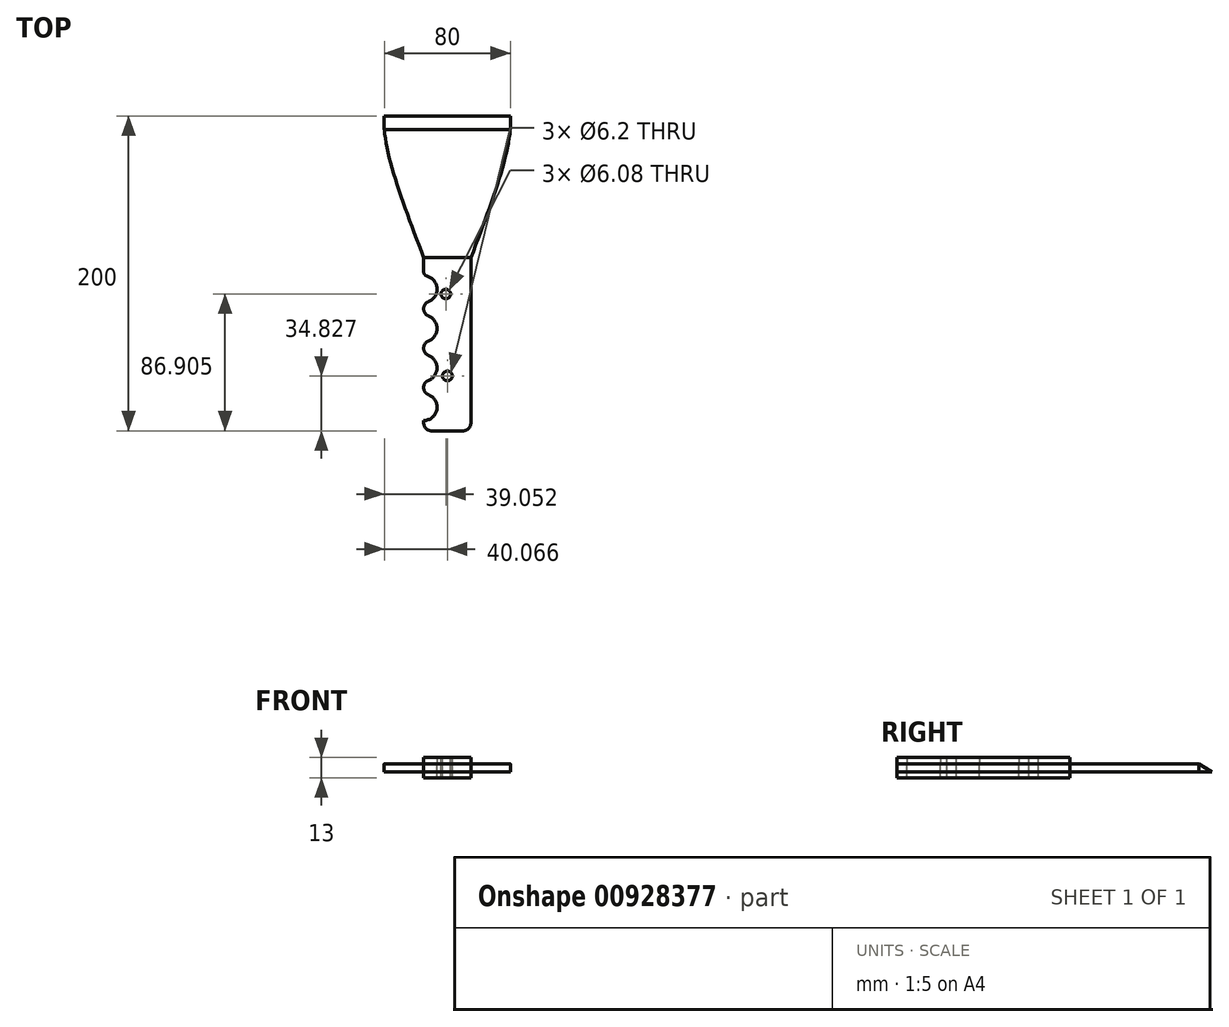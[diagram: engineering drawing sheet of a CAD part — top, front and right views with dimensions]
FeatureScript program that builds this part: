
annotation { "Feature Type Name" : "Feature", "Feature Type Description" : "" }
export const myFeature = defineFeature(function(context is Context, id is Id, definition is map)
    precondition{}
    {
        {
            var Q0;
            Q0=qCreatedBy(makeId("Top.planeOp"),FACE);
            var sketch = newSketch(context, id + "F0", { "sketchPlane" : qUnion([Q0])});
            skLineSegment(sketch, "E0.bottom", {"start": v(-36.21, -52.82) * mm, "end": v(43.79, -52.82) * mm});
            skLineSegment(sketch, "E0.top", {"start": v(-36.21, 147.18) * mm, "end": v(43.79, 147.18) * mm});
            skLineSegment(sketch, "E0.left", {"start": v(-36.21, -52.82) * mm, "end": v(-36.21, 147.18) * mm});
            skLineSegment(sketch, "E0.right", {"start": v(43.79, -52.82) * mm, "end": v(43.79, 147.18) * mm});
            skLineSegment(sketch, "E1.0", {"start": v(-36.21, 57.18) * mm, "end": v(43.79, 57.18) * mm});
            skLineSegment(sketch, "E2.0", {"start": v(18.79, -52.82) * mm, "end": v(18.79, 147.18) * mm});
            skLineSegment(sketch, "E3.0", {"start": v(-11.21, -52.82) * mm, "end": v(-11.21, 147.18) * mm});
            skFitSpline(sketch, "E4", {"points": [v(18.79, 57.18) * mm, v(43.79, 147.18) * mm, v(32.99, 168.62) * mm], "startDerivative": vector(60.83, 159.48) * mm, "endDerivative": vector(-43.84, 51.63) * mm});
            skFitSpline(sketch, "E5", {"points": [v(-11.21, 57.18) * mm, v(-36.21, 147.18) * mm, v(-25.14, 169.08) * mm], "startDerivative": vector(-61.11, 159.77) * mm, "endDerivative": vector(44.62, 52.51) * mm});
            skSolve(sketch);
        }
        {
            var Q0;
            {var subQ2=sQuery(id+"F0.wireOp",EDGE,"E0.top");var subQ4=sQuery(id+"F0.wireOp",EDGE,"E3.0");var subQ5=makeQuery(id+"F0.imprint","INTERSECT",VERTEX,{"derivedFrom":[subQ2,subQ4]});Q0=makeQuery(id+"F0.imprint","IMPRINT",FACE,{"disambiguationData":[TD([[makeQuery(id+"F0.imprint","IMPRINT",EDGE,{"disambiguationData":[TD([[subQ5,1.0]])],"derivedFrom":subQ2}),-1.0]])]});}
            var Q1;
            {var subQ0=sQuery(id+"F0.wireOp",EDGE,"E2.0");var subQ1=sQuery(id+"F0.wireOp",EDGE,"E0.top");var subQ2=makeQuery(id+"F0.imprint","INTERSECT",VERTEX,{"derivedFrom":[subQ1,subQ0]});Q1=makeQuery(id+"F0.imprint","IMPRINT",FACE,{"disambiguationData":[TD([[makeQuery(id+"F0.imprint","IMPRINT",EDGE,{"disambiguationData":[TD([[subQ2,1.0]])],"derivedFrom":subQ1}),-1.0]])]});}
            var Q2;
            {var subQ2=sQuery(id+"F0.wireOp",EDGE,"E0.top");var subQ4=sQuery(id+"F0.wireOp",EDGE,"E2.0");var subQ5=makeQuery(id+"F0.imprint","INTERSECT",VERTEX,{"derivedFrom":[subQ2,subQ4]});Q2=makeQuery(id+"F0.imprint","IMPRINT",FACE,{"disambiguationData":[TD([[makeQuery(id+"F0.imprint","IMPRINT",EDGE,{"disambiguationData":[TD([[subQ5,-1.0]])],"derivedFrom":subQ2}),-1.0]])]});}
            var Q3;
            {var subQ0=sQuery(id+"F0.wireOp",EDGE,"E2.0");var subQ1=sQuery(id+"F0.wireOp",EDGE,"E0.bottom");var subQ2=makeQuery(id+"F0.imprint","INTERSECT",VERTEX,{"derivedFrom":[subQ1,subQ0]});Q3=makeQuery(id+"F0.imprint","IMPRINT",FACE,{"disambiguationData":[TD([[makeQuery(id+"F0.imprint","IMPRINT",EDGE,{"disambiguationData":[TD([[subQ2,1.0]])],"derivedFrom":subQ1}),1.0]])]});}
            extrude(context, id + "F1", {"entities" : qUnion([Q0, Q1, Q2, Q3]), "depth" : 5 * mm, "offsetDistance" : 25 * mm});
        }
        {
            var Q0;
            Q0=makeQuery(id+"F1.opExtrude","CAP_FACE",FACE,{"disambiguationData":[OSD([sQuery(id+"F0.wireOp",EDGE,"E0.bottom"),sQuery(id+"F0.wireOp",EDGE,"E0.top"),sQuery(id+"F0.wireOp",EDGE,"E0.left"),sQuery(id+"F0.wireOp",EDGE,"E0.right"),sQuery(id+"F0.wireOp",EDGE,"E2.0"),sQuery(id+"F0.wireOp",EDGE,"E3.0"),sQuery(id+"F0.wireOp",EDGE,"E4"),sQuery(id+"F0.wireOp",EDGE,"E5")])],"isStart":false});
            var sketch = newSketch(context, id + "F2", { "sketchPlane" : qUnion([Q0])});
            skCircle(sketch, "E6", {"center": v(-11.21, 37.18) * mm, "radius": 8.5 * mm});
            skCircle(sketch, "E7", {"center": v(-11.21, 12.18) * mm, "radius": 8.5 * mm});
            skCircle(sketch, "E8", {"center": v(-11.21, -12.82) * mm, "radius": 8.5 * mm});
            skCircle(sketch, "E9", {"center": v(-11.21, -37.82) * mm, "radius": 8.5 * mm});
            skSolve(sketch);
        }
        {
            var Q0;
            Q0=makeQuery(id+"F1.opExtrude","SWEPT_EDGE",EDGE,{"disambiguationData":[OSD([sQuery(id+"F0.wireOp",EDGE,"E0.bottom"),sQuery(id+"F0.wireOp",EDGE,"E3.0")])]});
            var Q1;
            Q1=makeQuery(id+"F1.opExtrude","SWEPT_EDGE",EDGE,{"disambiguationData":[OSD([sQuery(id+"F0.wireOp",EDGE,"E0.bottom"),sQuery(id+"F0.wireOp",EDGE,"E2.0")])]});
            fillet(context, id + "F3", {"entities" : qUnion([Q0, Q1]), "radius" : 5 * mm, "tangentPropagation" : true, "allowEdgeOverflow" : false});
        }
        {
            var Q0;
            {var subQ0=sQuery(id+"F2.wireOp",EDGE,"E6");var subQ1=makeQuery(id+"F1.opExtrude","CAP_EDGE",EDGE,{"disambiguationData":[OSD([sQuery(id+"F0.wireOp",EDGE,"E3.0")])],"isStart":false});var subQ2=makeQuery(id+"F2.imprint","INTERSECT",VERTEX,{"disambiguationData":[OD(0.0)],"derivedFrom":[subQ1,subQ0]});Q0=makeQuery(id+"F2.imprint","IMPRINT",FACE,{"disambiguationData":[TD([[makeQuery(id+"F2.imprint","IMPRINT",EDGE,{"disambiguationData":[TD([[subQ2,1.0]])],"derivedFrom":subQ0}),1.0]])]});}
            var Q1;
            {var subQ0=sQuery(id+"F2.wireOp",EDGE,"E7");var subQ1=makeQuery(id+"F1.opExtrude","CAP_EDGE",EDGE,{"disambiguationData":[OSD([sQuery(id+"F0.wireOp",EDGE,"E3.0")])],"isStart":false});var subQ2=makeQuery(id+"F2.imprint","INTERSECT",VERTEX,{"disambiguationData":[OD(0.0)],"derivedFrom":[subQ1,subQ0]});Q1=makeQuery(id+"F2.imprint","IMPRINT",FACE,{"disambiguationData":[TD([[makeQuery(id+"F2.imprint","IMPRINT",EDGE,{"disambiguationData":[TD([[subQ2,1.0]])],"derivedFrom":subQ0}),1.0]])]});}
            var Q2;
            {var subQ0=sQuery(id+"F2.wireOp",EDGE,"E8");var subQ1=makeQuery(id+"F1.opExtrude","CAP_EDGE",EDGE,{"disambiguationData":[OSD([sQuery(id+"F0.wireOp",EDGE,"E3.0")])],"isStart":false});var subQ2=makeQuery(id+"F2.imprint","INTERSECT",VERTEX,{"disambiguationData":[OD(0.0)],"derivedFrom":[subQ1,subQ0]});Q2=makeQuery(id+"F2.imprint","IMPRINT",FACE,{"disambiguationData":[TD([[makeQuery(id+"F2.imprint","IMPRINT",EDGE,{"disambiguationData":[TD([[subQ2,-1.0]])],"derivedFrom":subQ0}),1.0]])]});}
            var Q3;
            {var subQ0=sQuery(id+"F2.wireOp",EDGE,"E9");var subQ1=makeQuery(id+"F1.opExtrude","CAP_EDGE",EDGE,{"disambiguationData":[OSD([sQuery(id+"F0.wireOp",EDGE,"E3.0")])],"isStart":false});var subQ2=makeQuery(id+"F2.imprint","INTERSECT",VERTEX,{"disambiguationData":[OD(0.0)],"derivedFrom":[subQ1,subQ0]});Q3=makeQuery(id+"F2.imprint","IMPRINT",FACE,{"disambiguationData":[TD([[makeQuery(id+"F2.imprint","IMPRINT",EDGE,{"disambiguationData":[TD([[subQ2,-1.0]])],"derivedFrom":subQ0}),1.0]])]});}
            extrude(context, id + "F4", {"entities" : qUnion([Q0, Q1, Q2, Q3]), "operationType" : NewBodyOperationType.REMOVE, "oppositeDirection" : true, "depth" : 25 * mm, "offsetDistance" : 25 * mm});
        }
        {
            var Q0;
            {var subQ0=sQuery(id+"F2.wireOp",EDGE,"E8");var subQ1=sQuery(id+"F0.wireOp",EDGE,"E3.0");Q0=makeQuery(id+"F4.boolean.opBoolean","COPY",EDGE,{"derivedFrom":makeQuery(id+"F4.opExtrude","SWEPT_EDGE",EDGE,{"disambiguationData":[OSD([subQ1,subQ0]),TDD([makeQuery(id+"F2.imprint","INTERSECT",VERTEX,{"disambiguationData":[OD(1.0)],"derivedFrom":[makeQuery(id+"F1.opExtrude","CAP_EDGE",EDGE,{"disambiguationData":[OSD([subQ1])],"isStart":false}),subQ0]})])]})});}
            var Q1;
            {var subQ0=sQuery(id+"F2.wireOp",EDGE,"E7");var subQ1=sQuery(id+"F0.wireOp",EDGE,"E3.0");Q1=makeQuery(id+"F4.boolean.opBoolean","COPY",EDGE,{"derivedFrom":makeQuery(id+"F4.opExtrude","SWEPT_EDGE",EDGE,{"disambiguationData":[OSD([subQ1,subQ0]),TDD([makeQuery(id+"F2.imprint","INTERSECT",VERTEX,{"disambiguationData":[OD(1.0)],"derivedFrom":[makeQuery(id+"F1.opExtrude","CAP_EDGE",EDGE,{"disambiguationData":[OSD([subQ1])],"isStart":false}),subQ0]})])]})});}
            var Q2;
            {var subQ0=sQuery(id+"F2.wireOp",EDGE,"E8");var subQ1=sQuery(id+"F0.wireOp",EDGE,"E3.0");Q2=makeQuery(id+"F4.boolean.opBoolean","COPY",EDGE,{"derivedFrom":makeQuery(id+"F4.opExtrude","SWEPT_EDGE",EDGE,{"disambiguationData":[OSD([subQ1,subQ0]),TDD([makeQuery(id+"F2.imprint","INTERSECT",VERTEX,{"disambiguationData":[OD(0.0)],"derivedFrom":[makeQuery(id+"F1.opExtrude","CAP_EDGE",EDGE,{"disambiguationData":[OSD([subQ1])],"isStart":false}),subQ0]})])]})});}
            var Q3;
            {var subQ0=sQuery(id+"F2.wireOp",EDGE,"E9");var subQ1=sQuery(id+"F0.wireOp",EDGE,"E3.0");Q3=makeQuery(id+"F4.boolean.opBoolean","COPY",EDGE,{"derivedFrom":makeQuery(id+"F4.opExtrude","SWEPT_EDGE",EDGE,{"disambiguationData":[OSD([subQ1,subQ0]),TDD([makeQuery(id+"F2.imprint","INTERSECT",VERTEX,{"disambiguationData":[OD(1.0)],"derivedFrom":[makeQuery(id+"F1.opExtrude","CAP_EDGE",EDGE,{"disambiguationData":[OSD([subQ1])],"isStart":false}),subQ0]})])]})});}
            var Q4;
            {var subQ0=sQuery(id+"F2.wireOp",EDGE,"E9");var subQ1=sQuery(id+"F0.wireOp",EDGE,"E3.0");Q4=makeQuery(id+"F4.boolean.opBoolean","COPY",EDGE,{"derivedFrom":makeQuery(id+"F4.opExtrude","SWEPT_EDGE",EDGE,{"disambiguationData":[OSD([subQ1,subQ0]),TDD([makeQuery(id+"F2.imprint","INTERSECT",VERTEX,{"disambiguationData":[OD(0.0)],"derivedFrom":[makeQuery(id+"F1.opExtrude","CAP_EDGE",EDGE,{"disambiguationData":[OSD([subQ1])],"isStart":false}),subQ0]})])]})});}
            var Q5;
            {var subQ0=sQuery(id+"F2.wireOp",EDGE,"E7");var subQ1=sQuery(id+"F0.wireOp",EDGE,"E3.0");Q5=makeQuery(id+"F4.boolean.opBoolean","COPY",EDGE,{"derivedFrom":makeQuery(id+"F4.opExtrude","SWEPT_EDGE",EDGE,{"disambiguationData":[OSD([subQ1,subQ0]),TDD([makeQuery(id+"F2.imprint","INTERSECT",VERTEX,{"disambiguationData":[OD(0.0)],"derivedFrom":[makeQuery(id+"F1.opExtrude","CAP_EDGE",EDGE,{"disambiguationData":[OSD([subQ1])],"isStart":false}),subQ0]})])]})});}
            var Q6;
            {var subQ0=sQuery(id+"F2.wireOp",EDGE,"E6");var subQ1=sQuery(id+"F0.wireOp",EDGE,"E3.0");Q6=makeQuery(id+"F4.boolean.opBoolean","COPY",EDGE,{"derivedFrom":makeQuery(id+"F4.opExtrude","SWEPT_EDGE",EDGE,{"disambiguationData":[OSD([subQ1,subQ0]),TDD([makeQuery(id+"F2.imprint","INTERSECT",VERTEX,{"disambiguationData":[OD(1.0)],"derivedFrom":[makeQuery(id+"F1.opExtrude","CAP_EDGE",EDGE,{"disambiguationData":[OSD([subQ1])],"isStart":false}),subQ0]})])]})});}
            fillet(context, id + "F5", {"entities" : qUnion([Q0, Q1, Q2, Q3, Q4, Q5, Q6]), "radius" : 5 * mm, "tangentPropagation" : true, "allowEdgeOverflow" : false});
        }
        {
            var Q0;
            {var subQ0=sQuery(id+"F2.wireOp",EDGE,"E8");var subQ1=sQuery(id+"F0.wireOp",EDGE,"E3.0");Q0=makeQuery(id+"F4.boolean.opBoolean","COPY",EDGE,{"derivedFrom":makeQuery(id+"F4.opExtrude","SWEPT_EDGE",EDGE,{"disambiguationData":[OSD([subQ1,subQ0]),TDD([makeQuery(id+"F2.imprint","INTERSECT",VERTEX,{"disambiguationData":[OD(0.0)],"derivedFrom":[makeQuery(id+"F1.opExtrude","CAP_EDGE",EDGE,{"disambiguationData":[OSD([subQ1])],"isStart":false}),subQ0]})])]})});}
            var Q1;
            {var subQ0=sQuery(id+"F2.wireOp",EDGE,"E9");var subQ1=sQuery(id+"F0.wireOp",EDGE,"E3.0");Q1=makeQuery(id+"F4.boolean.opBoolean","COPY",EDGE,{"derivedFrom":makeQuery(id+"F4.opExtrude","SWEPT_EDGE",EDGE,{"disambiguationData":[OSD([subQ1,subQ0]),TDD([makeQuery(id+"F2.imprint","INTERSECT",VERTEX,{"disambiguationData":[OD(1.0)],"derivedFrom":[makeQuery(id+"F1.opExtrude","CAP_EDGE",EDGE,{"disambiguationData":[OSD([subQ1])],"isStart":false}),subQ0]})])]})});}
            var Q2;
            {var subQ0=sQuery(id+"F2.wireOp",EDGE,"E9");var subQ1=sQuery(id+"F0.wireOp",EDGE,"E3.0");Q2=makeQuery(id+"F4.boolean.opBoolean","COPY",EDGE,{"derivedFrom":makeQuery(id+"F4.opExtrude","SWEPT_EDGE",EDGE,{"disambiguationData":[OSD([subQ1,subQ0]),TDD([makeQuery(id+"F2.imprint","INTERSECT",VERTEX,{"disambiguationData":[OD(0.0)],"derivedFrom":[makeQuery(id+"F1.opExtrude","CAP_EDGE",EDGE,{"disambiguationData":[OSD([subQ1])],"isStart":false}),subQ0]})])]})});}
            var Q3;
            {var subQ0=sQuery(id+"F2.wireOp",EDGE,"E7");var subQ1=sQuery(id+"F0.wireOp",EDGE,"E3.0");Q3=makeQuery(id+"F4.boolean.opBoolean","COPY",EDGE,{"derivedFrom":makeQuery(id+"F4.opExtrude","SWEPT_EDGE",EDGE,{"disambiguationData":[OSD([subQ1,subQ0]),TDD([makeQuery(id+"F2.imprint","INTERSECT",VERTEX,{"disambiguationData":[OD(1.0)],"derivedFrom":[makeQuery(id+"F1.opExtrude","CAP_EDGE",EDGE,{"disambiguationData":[OSD([subQ1])],"isStart":false}),subQ0]})])]})});}
            var Q4;
            {var subQ0=sQuery(id+"F2.wireOp",EDGE,"E8");var subQ1=sQuery(id+"F0.wireOp",EDGE,"E3.0");Q4=makeQuery(id+"F4.boolean.opBoolean","COPY",EDGE,{"derivedFrom":makeQuery(id+"F4.opExtrude","SWEPT_EDGE",EDGE,{"disambiguationData":[OSD([subQ1,subQ0]),TDD([makeQuery(id+"F2.imprint","INTERSECT",VERTEX,{"disambiguationData":[OD(1.0)],"derivedFrom":[makeQuery(id+"F1.opExtrude","CAP_EDGE",EDGE,{"disambiguationData":[OSD([subQ1])],"isStart":false}),subQ0]})])]})});}
            var Q5;
            {var subQ0=sQuery(id+"F2.wireOp",EDGE,"E7");var subQ1=sQuery(id+"F0.wireOp",EDGE,"E3.0");Q5=makeQuery(id+"F4.boolean.opBoolean","COPY",EDGE,{"derivedFrom":makeQuery(id+"F4.opExtrude","SWEPT_EDGE",EDGE,{"disambiguationData":[OSD([subQ1,subQ0]),TDD([makeQuery(id+"F2.imprint","INTERSECT",VERTEX,{"disambiguationData":[OD(0.0)],"derivedFrom":[makeQuery(id+"F1.opExtrude","CAP_EDGE",EDGE,{"disambiguationData":[OSD([subQ1])],"isStart":false}),subQ0]})])]})});}
            var Q6;
            {var subQ0=sQuery(id+"F2.wireOp",EDGE,"E6");var subQ1=sQuery(id+"F0.wireOp",EDGE,"E3.0");Q6=makeQuery(id+"F4.boolean.opBoolean","COPY",EDGE,{"derivedFrom":makeQuery(id+"F4.opExtrude","SWEPT_EDGE",EDGE,{"disambiguationData":[OSD([subQ1,subQ0]),TDD([makeQuery(id+"F2.imprint","INTERSECT",VERTEX,{"disambiguationData":[OD(0.0)],"derivedFrom":[makeQuery(id+"F1.opExtrude","CAP_EDGE",EDGE,{"disambiguationData":[OSD([subQ1])],"isStart":false}),subQ0]})])]})});}
            var Q7;
            {var subQ0=sQuery(id+"F2.wireOp",EDGE,"E6");var subQ1=sQuery(id+"F0.wireOp",EDGE,"E3.0");Q7=makeQuery(id+"F4.boolean.opBoolean","COPY",EDGE,{"derivedFrom":makeQuery(id+"F4.opExtrude","SWEPT_EDGE",EDGE,{"disambiguationData":[OSD([subQ1,subQ0]),TDD([makeQuery(id+"F2.imprint","INTERSECT",VERTEX,{"disambiguationData":[OD(1.0)],"derivedFrom":[makeQuery(id+"F1.opExtrude","CAP_EDGE",EDGE,{"disambiguationData":[OSD([subQ1])],"isStart":false}),subQ0]})])]})});}
            fillet(context, id + "F6", {"entities" : qUnion([Q0, Q1, Q2, Q3, Q4, Q5, Q6, Q7]), "radius" : 3 * mm, "tangentPropagation" : true, "allowEdgeOverflow" : false});
        }
        {
            var Q0;
            Q0=makeQuery(id+"F1.opExtrude","CAP_EDGE",EDGE,{"disambiguationData":[OSD([sQuery(id+"F0.wireOp",EDGE,"E0.top")])],"isStart":false});
            chamfer(context, id + "F7", {"entities" : qUnion([Q0]), "chamferType" : ChamferType.OFFSET_ANGLE, "width" : 5 * mm, "oppositeDirection" : false, "angle" : 60 * degree, "tangentPropagation" : true});
        }
        {
            var Q0;
            Q0=makeQuery(id+"F1.opExtrude","CAP_FACE",FACE,{"disambiguationData":[OSD([sQuery(id+"F0.wireOp",EDGE,"E0.bottom"),sQuery(id+"F0.wireOp",EDGE,"E0.top"),sQuery(id+"F0.wireOp",EDGE,"E0.left"),sQuery(id+"F0.wireOp",EDGE,"E0.right"),sQuery(id+"F0.wireOp",EDGE,"E2.0"),sQuery(id+"F0.wireOp",EDGE,"E3.0"),sQuery(id+"F0.wireOp",EDGE,"E4"),sQuery(id+"F0.wireOp",EDGE,"E5")])],"isStart":false});
            var sketch = newSketch(context, id + "F8", { "sketchPlane" : qUnion([Q0])});
            skLineSegment(sketch, "E10", {"start": v(-11.21, 57.18) * mm, "end": v(18.79, 57.18) * mm});
            skSolve(sketch);
        }
        {
            var Q0;
            Q0=makeQuery(id+"F8.imprint","IMPRINT",FACE,{"disambiguationData":[TD([[makeQuery(id+"F8.imprint","IMPRINT",EDGE,{"derivedFrom":sQuery(id+"F8.wireOp",EDGE,"E10")}),-1.0]])]});
            extrude(context, id + "F9", {"entities" : qUnion([Q0]), "depth" : 4 * mm, "offsetDistance" : 25 * mm});
        }
        {
            var Q0;
            Q0=makeQuery(id+"F1.opExtrude","CAP_FACE",FACE,{"disambiguationData":[OSD([sQuery(id+"F0.wireOp",EDGE,"E0.bottom"),sQuery(id+"F0.wireOp",EDGE,"E0.top"),sQuery(id+"F0.wireOp",EDGE,"E0.left"),sQuery(id+"F0.wireOp",EDGE,"E0.right"),sQuery(id+"F0.wireOp",EDGE,"E2.0"),sQuery(id+"F0.wireOp",EDGE,"E3.0"),sQuery(id+"F0.wireOp",EDGE,"E4"),sQuery(id+"F0.wireOp",EDGE,"E5")])],"isStart":true});
            var sketch = newSketch(context, id + "F10", { "sketchPlane" : qUnion([Q0])});
            skLineSegment(sketch, "E11", {"start": v(18.79, -57.18) * mm, "end": v(-11.21, -57.18) * mm});
            skSolve(sketch);
        }
        {
            var Q0;
            Q0=makeQuery(id+"F10.imprint","IMPRINT",FACE,{"disambiguationData":[TD([[makeQuery(id+"F10.imprint","IMPRINT",EDGE,{"derivedFrom":sQuery(id+"F10.wireOp",EDGE,"E11")}),-1.0]])]});
            extrude(context, id + "F11", {"entities" : qUnion([Q0]), "depth" : 4 * mm, "offsetDistance" : 25 * mm});
        }
        {
            var Q0;
            Q0=makeQuery(id+"F9.opExtrude","CAP_FACE",FACE,{"disambiguationData":[OSD([sQuery(id+"F0.wireOp",EDGE,"E0.bottom"),sQuery(id+"F0.wireOp",EDGE,"E0.top"),sQuery(id+"F0.wireOp",EDGE,"E0.left"),sQuery(id+"F0.wireOp",EDGE,"E0.right"),sQuery(id+"F0.wireOp",EDGE,"E2.0"),sQuery(id+"F0.wireOp",EDGE,"E3.0"),sQuery(id+"F0.wireOp",EDGE,"E4"),sQuery(id+"F0.wireOp",EDGE,"E5"),sQuery(id+"F2.wireOp",EDGE,"E6"),sQuery(id+"F2.wireOp",EDGE,"E7"),sQuery(id+"F2.wireOp",EDGE,"E8"),sQuery(id+"F2.wireOp",EDGE,"E9"),sQuery(id+"F8.wireOp",EDGE,"E10")])],"isStart":false});
            var sketch = newSketch(context, id + "F12", { "sketchPlane" : qUnion([Q0])});
            skCircle(sketch, "E12", {"center": v(2.84, 34.09) * mm, "radius": 3.04 * mm});
            skCircle(sketch, "E13", {"center": v(3.86, -18) * mm, "radius": 3.1 * mm});
            skSolve(sketch);
        }
        {
            var Q0;
            Q0=makeQuery(id+"F12.imprint","IMPRINT",FACE,{"disambiguationData":[TD([[makeQuery(id+"F12.imprint","IMPRINT",EDGE,{"derivedFrom":sQuery(id+"F12.wireOp",EDGE,"E12")}),1.0]])]});
            var Q1;
            Q1=makeQuery(id+"F12.imprint","IMPRINT",FACE,{"disambiguationData":[TD([[makeQuery(id+"F12.imprint","IMPRINT",EDGE,{"derivedFrom":sQuery(id+"F12.wireOp",EDGE,"E13")}),1.0]])]});
            extrude(context, id + "F13", {"entities" : qUnion([Q0, Q1]), "operationType" : NewBodyOperationType.REMOVE, "oppositeDirection" : true, "depth" : 25 * mm, "offsetDistance" : 25 * mm});
        }
    });
